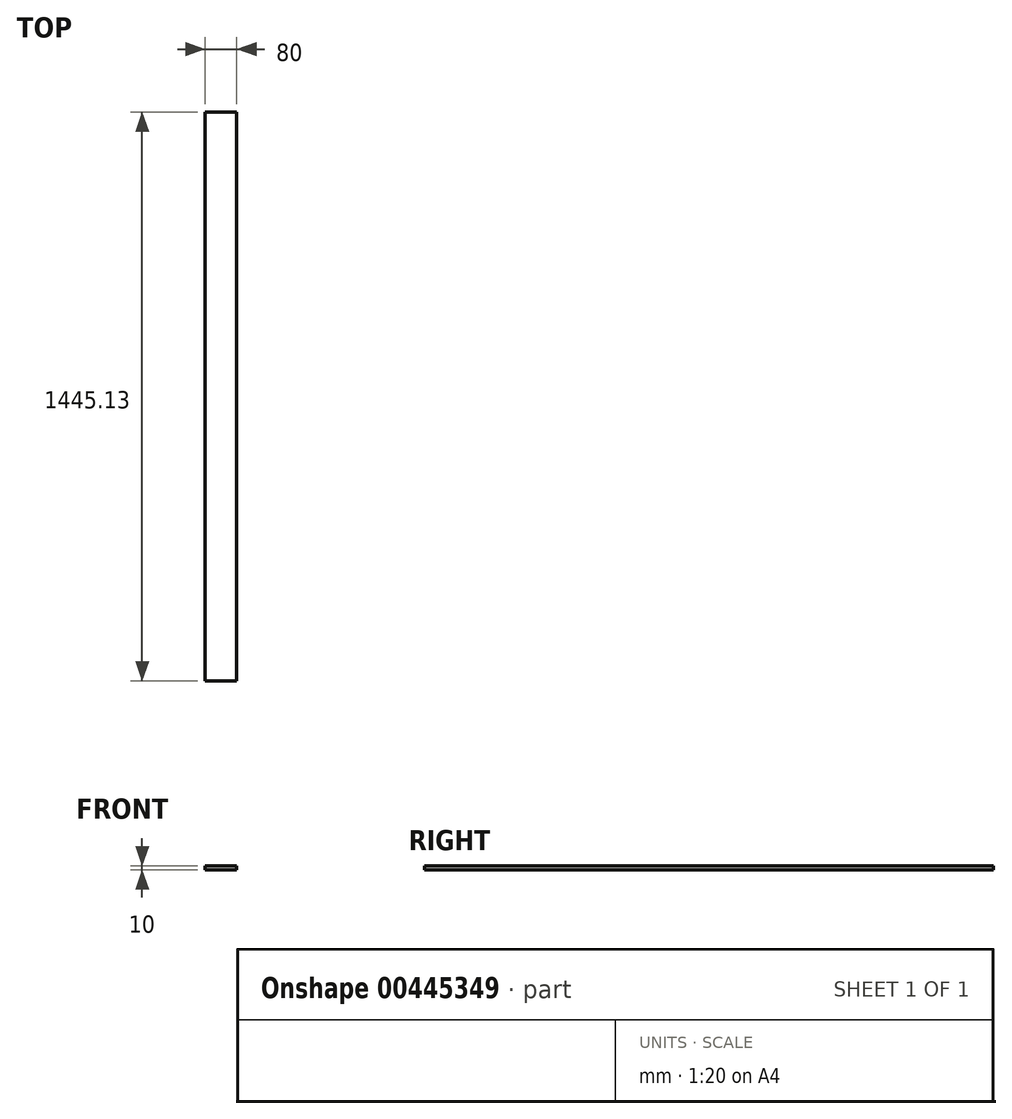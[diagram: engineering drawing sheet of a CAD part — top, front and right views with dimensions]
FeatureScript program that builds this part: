
annotation { "Feature Type Name" : "Feature", "Feature Type Description" : "" }
export const myFeature = defineFeature(function(context is Context, id is Id, definition is map)
    precondition{}
    {
        {
            var Q0;
            Q0=qCreatedBy(makeId("Top.planeOp"),FACE);
            var sketch = newSketch(context, id + "F0", { "sketchPlane" : qUnion([Q0])});
            skLineSegment(sketch, "E0.bottom", {"start": v(0, 0) * mm, "end": v(80, 0) * mm});
            skLineSegment(sketch, "E0.top", {"start": v(0, 1445.13) * mm, "end": v(80, 1445.13) * mm});
            skLineSegment(sketch, "E0.left", {"start": v(0, 0) * mm, "end": v(0, 1445.13) * mm});
            skLineSegment(sketch, "E0.right", {"start": v(80, 0) * mm, "end": v(80, 1445.13) * mm});
            skSolve(sketch);
        }
        {
            var Q0;
            Q0 = qSketchRegion(id + "F0", true);
            extrude(context, id + "F1", {"entities" : qUnion([Q0]), "depth" : 10 * mm});
        }
    });
